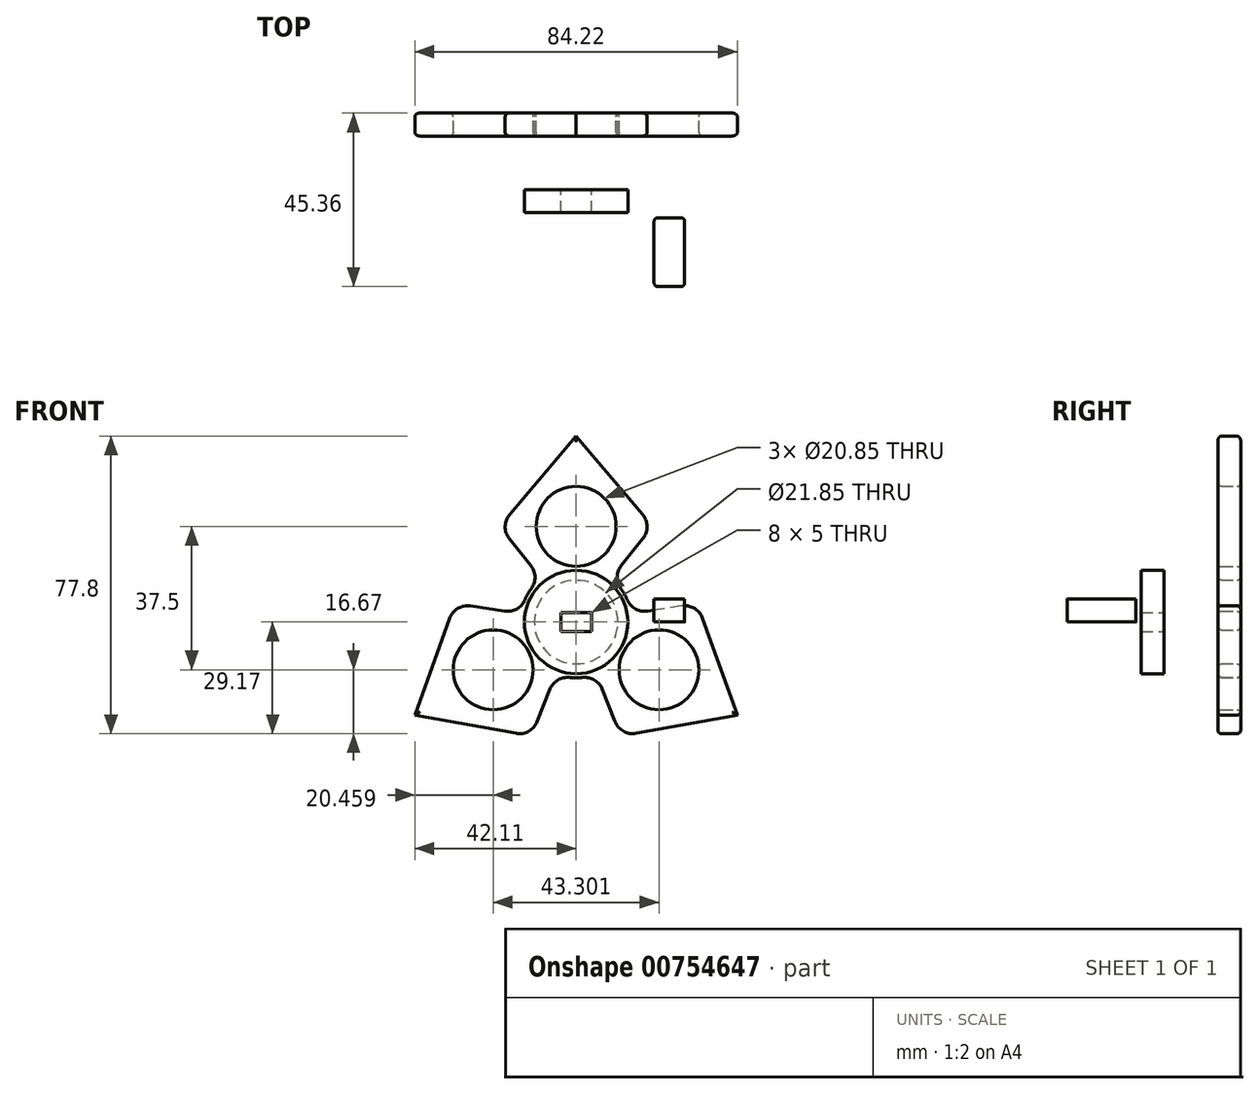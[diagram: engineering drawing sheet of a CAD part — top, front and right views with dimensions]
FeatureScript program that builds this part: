
annotation { "Feature Type Name" : "Feature", "Feature Type Description" : "" }
export const myFeature = defineFeature(function(context is Context, id is Id, definition is map)
    precondition{}
    {
        {
            var Q0;
            Q0=qCreatedBy(makeId("Front.planeOp"),FACE);
            var sketch = newSketch(context, id + "F0", { "sketchPlane" : qUnion([Q0])});
            skCircle(sketch, "E0", {"center": v(0, 0) * mm, "radius": 10.93 * mm});
            skArc(sketch, "E1", {"start": v(-1.5, 35.32) * mm, "mid": v(0, 14.58) * mm, "end": v(1.5, 35.32) * mm});
            skCircle(sketch, "E2", {"center": v(0, 25) * mm, "radius": 10.42 * mm});
            skCircle(sketch, "E3.1.0", {"center": v(-21.65, -12.5) * mm, "radius": 10.42 * mm});
            skCircle(sketch, "E3.2.0", {"center": v(21.65, -12.5) * mm, "radius": 10.42 * mm});
            skLineSegment(sketch, "E4", {"start": v(0, 25) * mm, "end": v(20, 25) * mm, "construction": true});
            skLineSegment(sketch, "E5", {"start": v(17.34, 28.14) * mm, "end": v(0, 48.63) * mm});
            skLineSegment(sketch, "E6", {"start": v(0, 25) * mm, "end": v(-20, 25) * mm, "construction": true});
            skLineSegment(sketch, "E7", {"start": v(-17.34, 28.14) * mm, "end": v(0, 48.63) * mm});
            skArc(sketch, "E8", {"start": v(-11.7, 8.68) * mm, "mid": v(-12.62, 7.29) * mm, "end": v(-13.37, 5.8) * mm});
            skLineSegment(sketch, "E9", {"start": v(17.43, 21.79) * mm, "end": v(11.82, 14.78) * mm});
            skLineSegment(sketch, "E10", {"start": v(-17.43, 21.79) * mm, "end": v(-11.82, 14.78) * mm});
            skLineSegment(sketch, "E11.1.0", {"start": v(-33.04, 0.95) * mm, "end": v(-42.11, -24.31) * mm});
            skLineSegment(sketch, "E11.1.1", {"start": v(-15.7, -29.09) * mm, "end": v(-42.11, -24.31) * mm});
            skLineSegment(sketch, "E11.1.2", {"start": v(-10.15, -25.99) * mm, "end": v(-6.89, -17.63) * mm});
            skLineSegment(sketch, "E11.1.3", {"start": v(-27.58, 4.2) * mm, "end": v(-18.7, 2.85) * mm});
            skLineSegment(sketch, "E11.2.0", {"start": v(15.7, -29.09) * mm, "end": v(42.11, -24.31) * mm});
            skLineSegment(sketch, "E11.2.1", {"start": v(33.04, 0.95) * mm, "end": v(42.11, -24.31) * mm});
            skLineSegment(sketch, "E11.2.2", {"start": v(27.58, 4.2) * mm, "end": v(18.7, 2.85) * mm});
            skLineSegment(sketch, "E11.2.3", {"start": v(10.15, -25.99) * mm, "end": v(6.89, -17.63) * mm});
            skArc(sketch, "E12.trimOffspring", {"start": v(13.37, 5.8) * mm, "mid": v(12.62, 7.29) * mm, "end": v(11.7, 8.68) * mm});
            skArc(sketch, "E13.trimOffspring", {"start": v(-1.66, -14.48) * mm, "mid": v(0, -14.57) * mm, "end": v(1.66, -14.48) * mm});
            skPoint(sketch, "E14.visualSharp", {"position": v(9.1, 11.38) * mm});
            skArc(sketch, "E14.filletArc", {"start": v(11.82, 14.78) * mm, "mid": v(10.73, 11.75) * mm, "end": v(11.7, 8.68) * mm});
            skPoint(sketch, "E15.visualSharp", {"position": v(14.4, 2.2) * mm});
            skArc(sketch, "E15.filletArc", {"start": v(13.37, 5.8) * mm, "mid": v(15.54, 3.42) * mm, "end": v(18.7, 2.85) * mm});
            skPoint(sketch, "E16.visualSharp", {"position": v(5.3, -13.58) * mm});
            skArc(sketch, "E16.filletArc", {"start": v(6.89, -17.63) * mm, "mid": v(4.8, -15.16) * mm, "end": v(1.66, -14.48) * mm});
            skPoint(sketch, "E17.visualSharp", {"position": v(-5.3, -13.58) * mm});
            skArc(sketch, "E17.filletArc", {"start": v(-1.66, -14.48) * mm, "mid": v(-4.8, -15.16) * mm, "end": v(-6.89, -17.63) * mm});
            skPoint(sketch, "E18.visualSharp", {"position": v(-9.1, 11.38) * mm});
            skArc(sketch, "E18.filletArc", {"start": v(-11.7, 8.68) * mm, "mid": v(-10.73, 11.75) * mm, "end": v(-11.82, 14.78) * mm});
            skPoint(sketch, "E19.visualSharp", {"position": v(-14.4, 2.2) * mm});
            skArc(sketch, "E19.filletArc", {"start": v(-18.7, 2.85) * mm, "mid": v(-15.54, 3.42) * mm, "end": v(-13.37, 5.8) * mm});
            skPoint(sketch, "E20.visualSharp", {"position": v(20, 25) * mm});
            skArc(sketch, "E20.filletArc", {"start": v(17.43, 21.79) * mm, "mid": v(18.52, 24.98) * mm, "end": v(17.34, 28.14) * mm});
            skPoint(sketch, "E21.visualSharp", {"position": v(-20, 25) * mm});
            skArc(sketch, "E21.filletArc", {"start": v(-17.34, 28.14) * mm, "mid": v(-18.52, 24.98) * mm, "end": v(-17.43, 21.79) * mm});
            skPoint(sketch, "E22.visualSharp", {"position": v(31.65, 4.82) * mm});
            skArc(sketch, "E22.filletArc", {"start": v(33.04, 0.95) * mm, "mid": v(30.9, 3.55) * mm, "end": v(27.58, 4.2) * mm});
            skPoint(sketch, "E23.visualSharp", {"position": v(11.65, -29.82) * mm});
            skArc(sketch, "E23.filletArc", {"start": v(10.15, -25.99) * mm, "mid": v(12.37, -28.53) * mm, "end": v(15.7, -29.09) * mm});
            skPoint(sketch, "E24.visualSharp", {"position": v(-11.65, -29.82) * mm});
            skArc(sketch, "E24.filletArc", {"start": v(-15.7, -29.09) * mm, "mid": v(-12.37, -28.53) * mm, "end": v(-10.15, -25.99) * mm});
            skPoint(sketch, "E25.visualSharp", {"position": v(-31.65, 4.82) * mm});
            skArc(sketch, "E25.filletArc", {"start": v(-27.58, 4.2) * mm, "mid": v(-30.9, 3.55) * mm, "end": v(-33.04, 0.95) * mm});
            skSolve(sketch);
        }
        {
            var Q0;
            Q0=makeQuery(id+"F0.imprint","IMPRINT",FACE,{"disambiguationData":[TD([[makeQuery(id+"F0.imprint","IMPRINT",EDGE,{"derivedFrom":sQuery(id+"F0.wireOp",EDGE,"E0")}),-1.0]])]});
            extrude(context, id + "F1", {"entities" : qUnion([Q0]), "depth" : 6 * mm, "offsetDistance" : 25 * mm});
        }
        {
            var Q0;
            Q0=makeQuery(id+"F1.opExtrude","CAP_FACE",FACE,{"disambiguationData":[OSD([sQuery(id+"F0.wireOp",EDGE,"E0"),sQuery(id+"F0.wireOp",EDGE,"E1"),sQuery(id+"F0.wireOp",EDGE,"6345f1c2-771f-4573-b072-38c9fe25f44f.1.0"),sQuery(id+"F0.wireOp",EDGE,"6345f1c2-771f-4573-b072-38c9fe25f44f.2.0"),sQuery(id+"F0.wireOp",EDGE,"6345f1c2-771f-4573-b072-38c9fe25f44f.3.0"),sQuery(id+"F0.wireOp",EDGE,"6345f1c2-771f-4573-b072-38c9fe25f44f.4.0"),sQuery(id+"F0.wireOp",EDGE,"6w4LuyIg-Judz-7qcx-iNhM-kCVs0XRHMAQz.left"),sQuery(id+"F0.wireOp",EDGE,"6w4LuyIg-Judz-7qcx-iNhM-kCVs0XRHMAQz.right"),sQuery(id+"F0.wireOp",EDGE,"GuxD1Two-tXSI-jhGi-diOq-QsG6SmieNdRW"),sQuery(id+"F0.wireOp",EDGE,"9e989a9f-be13-4d0f-822f-95c7c0624428.1.0"),sQuery(id+"F0.wireOp",EDGE,"9e989a9f-be13-4d0f-822f-95c7c0624428.1.1"),sQuery(id+"F0.wireOp",EDGE,"9e989a9f-be13-4d0f-822f-95c7c0624428.1.2"),sQuery(id+"F0.wireOp",EDGE,"9e989a9f-be13-4d0f-822f-95c7c0624428.2.0"),sQuery(id+"F0.wireOp",EDGE,"9e989a9f-be13-4d0f-822f-95c7c0624428.2.1"),sQuery(id+"F0.wireOp",EDGE,"9e989a9f-be13-4d0f-822f-95c7c0624428.2.2"),sQuery(id+"F0.wireOp",EDGE,"9e989a9f-be13-4d0f-822f-95c7c0624428.3.0"),sQuery(id+"F0.wireOp",EDGE,"9e989a9f-be13-4d0f-822f-95c7c0624428.3.1"),sQuery(id+"F0.wireOp",EDGE,"9e989a9f-be13-4d0f-822f-95c7c0624428.3.2"),sQuery(id+"F0.wireOp",EDGE,"9e989a9f-be13-4d0f-822f-95c7c0624428.4.0"),sQuery(id+"F0.wireOp",EDGE,"9e989a9f-be13-4d0f-822f-95c7c0624428.4.1"),sQuery(id+"F0.wireOp",EDGE,"9e989a9f-be13-4d0f-822f-95c7c0624428.4.2"),sQuery(id+"F0.wireOp",EDGE,"486a15bc-75c9-41d0-808c-e5c4775e6e80.filletArc"),sQuery(id+"F0.wireOp",EDGE,"d314a861-2769-46d2-9bec-117903992242.filletArc"),sQuery(id+"F0.wireOp",EDGE,"5d220be9-c9be-4508-b7a3-f434c5fdea58.filletArc"),sQuery(id+"F0.wireOp",EDGE,"2974d6c2-e4a2-45df-9bc2-224e587c2884.filletArc"),sQuery(id+"F0.wireOp",EDGE,"3265ed39-f9f2-4246-9e43-8a9d8c4dec78.filletArc")])],"isStart":false});
            var Q1;
            Q1=makeQuery(id+"F1.opExtrude","CAP_FACE",FACE,{"disambiguationData":[OSD([sQuery(id+"F0.wireOp",EDGE,"E0"),sQuery(id+"F0.wireOp",EDGE,"E1"),sQuery(id+"F0.wireOp",EDGE,"6345f1c2-771f-4573-b072-38c9fe25f44f.1.0"),sQuery(id+"F0.wireOp",EDGE,"6345f1c2-771f-4573-b072-38c9fe25f44f.2.0"),sQuery(id+"F0.wireOp",EDGE,"6345f1c2-771f-4573-b072-38c9fe25f44f.3.0"),sQuery(id+"F0.wireOp",EDGE,"6345f1c2-771f-4573-b072-38c9fe25f44f.4.0"),sQuery(id+"F0.wireOp",EDGE,"6w4LuyIg-Judz-7qcx-iNhM-kCVs0XRHMAQz.left"),sQuery(id+"F0.wireOp",EDGE,"6w4LuyIg-Judz-7qcx-iNhM-kCVs0XRHMAQz.right"),sQuery(id+"F0.wireOp",EDGE,"GuxD1Two-tXSI-jhGi-diOq-QsG6SmieNdRW"),sQuery(id+"F0.wireOp",EDGE,"9e989a9f-be13-4d0f-822f-95c7c0624428.1.0"),sQuery(id+"F0.wireOp",EDGE,"9e989a9f-be13-4d0f-822f-95c7c0624428.1.1"),sQuery(id+"F0.wireOp",EDGE,"9e989a9f-be13-4d0f-822f-95c7c0624428.1.2"),sQuery(id+"F0.wireOp",EDGE,"9e989a9f-be13-4d0f-822f-95c7c0624428.2.0"),sQuery(id+"F0.wireOp",EDGE,"9e989a9f-be13-4d0f-822f-95c7c0624428.2.1"),sQuery(id+"F0.wireOp",EDGE,"9e989a9f-be13-4d0f-822f-95c7c0624428.2.2"),sQuery(id+"F0.wireOp",EDGE,"9e989a9f-be13-4d0f-822f-95c7c0624428.3.0"),sQuery(id+"F0.wireOp",EDGE,"9e989a9f-be13-4d0f-822f-95c7c0624428.3.1"),sQuery(id+"F0.wireOp",EDGE,"9e989a9f-be13-4d0f-822f-95c7c0624428.3.2"),sQuery(id+"F0.wireOp",EDGE,"9e989a9f-be13-4d0f-822f-95c7c0624428.4.0"),sQuery(id+"F0.wireOp",EDGE,"9e989a9f-be13-4d0f-822f-95c7c0624428.4.1"),sQuery(id+"F0.wireOp",EDGE,"9e989a9f-be13-4d0f-822f-95c7c0624428.4.2"),sQuery(id+"F0.wireOp",EDGE,"486a15bc-75c9-41d0-808c-e5c4775e6e80.filletArc"),sQuery(id+"F0.wireOp",EDGE,"d314a861-2769-46d2-9bec-117903992242.filletArc"),sQuery(id+"F0.wireOp",EDGE,"5d220be9-c9be-4508-b7a3-f434c5fdea58.filletArc"),sQuery(id+"F0.wireOp",EDGE,"2974d6c2-e4a2-45df-9bc2-224e587c2884.filletArc"),sQuery(id+"F0.wireOp",EDGE,"3265ed39-f9f2-4246-9e43-8a9d8c4dec78.filletArc")])],"isStart":true});
            fillet(context, id + "F2", {"entities" : qUnion([Q0, Q1]), "radius" : 1 * mm, "tangentPropagation" : true, "allowEdgeOverflow" : false});
        }
        {
            var Q0;
            Q0=qCreatedBy(makeId("Top.planeOp"),FACE);
            var sketch = newSketch(context, id + "F3", { "sketchPlane" : qUnion([Q0])});
            skLineSegment(sketch, "E26.bottom", {"start": v(21.35, -27.36) * mm, "end": v(27.35, -27.36) * mm});
            skLineSegment(sketch, "E26.top", {"start": v(21.35, -45.36) * mm, "end": v(27.35, -45.36) * mm});
            skLineSegment(sketch, "E26.left", {"start": v(20.35, -28.36) * mm, "end": v(20.35, -44.36) * mm});
            skLineSegment(sketch, "E26.right", {"start": v(28.35, -28.36) * mm, "end": v(28.35, -44.36) * mm});
            skPoint(sketch, "E26.middle", {"position": v(24.35, -36.36) * mm});
            skPoint(sketch, "E27.visualSharp", {"position": v(20.35, -45.36) * mm});
            skArc(sketch, "E27.filletArc", {"start": v(20.35, -44.36) * mm, "mid": v(20.64, -45.06) * mm, "end": v(21.35, -45.36) * mm});
            skPoint(sketch, "E28.visualSharp", {"position": v(28.35, -45.36) * mm});
            skArc(sketch, "E28.filletArc", {"start": v(27.35, -45.36) * mm, "mid": v(28.05, -45.06) * mm, "end": v(28.35, -44.36) * mm});
            skPoint(sketch, "E29.visualSharp", {"position": v(28.35, -27.36) * mm});
            skArc(sketch, "E29.filletArc", {"start": v(28.35, -28.36) * mm, "mid": v(28.05, -27.65) * mm, "end": v(27.35, -27.36) * mm});
            skPoint(sketch, "E30.visualSharp", {"position": v(20.35, -27.36) * mm});
            skArc(sketch, "E30.filletArc", {"start": v(21.35, -27.36) * mm, "mid": v(20.64, -27.65) * mm, "end": v(20.35, -28.36) * mm});
            skSolve(sketch);
        }
        {
            var Q0;
            Q0=makeQuery(id+"F3.imprint","IMPRINT",FACE,{"disambiguationData":[TD([[makeQuery(id+"F3.imprint","IMPRINT",EDGE,{"derivedFrom":sQuery(id+"F3.wireOp",EDGE,"E26.bottom")}),-1.0]])]});
            extrude(context, id + "F4", {"entities" : qUnion([Q0]), "depth" : 6 * mm, "offsetDistance" : 25 * mm});
        }
        {
            var Q0;
            Q0=qCreatedBy(makeId("Front.planeOp"),FACE);
            var sketch = newSketch(context, id + "F5", { "sketchPlane" : qUnion([Q0])});
            skCircle(sketch, "E31", {"center": v(0, 0) * mm, "radius": 13.5 * mm});
            skLineSegment(sketch, "E32.bottom", {"start": v(4, -2.5) * mm, "end": v(-4, -2.5) * mm});
            skLineSegment(sketch, "E32.top", {"start": v(4, 2.5) * mm, "end": v(-4, 2.5) * mm});
            skLineSegment(sketch, "E32.left", {"start": v(4, -2.5) * mm, "end": v(4, 2.5) * mm});
            skLineSegment(sketch, "E32.right", {"start": v(-4, -2.5) * mm, "end": v(-4, 2.5) * mm});
            skSolve(sketch);
        }
        {
            var Q0;
            Q0=qSketchRegion(id+"F5",true);
            extrude(context, id + "F6", {"entities" : qUnion([Q0]), "depth" : 26 * mm, "offsetDistance" : 25 * mm, "hasSecondDirection" : true, "secondDirectionOppositeDirection" : false, "secondDirectionDepth" : 20 * mm});
        }
    });
